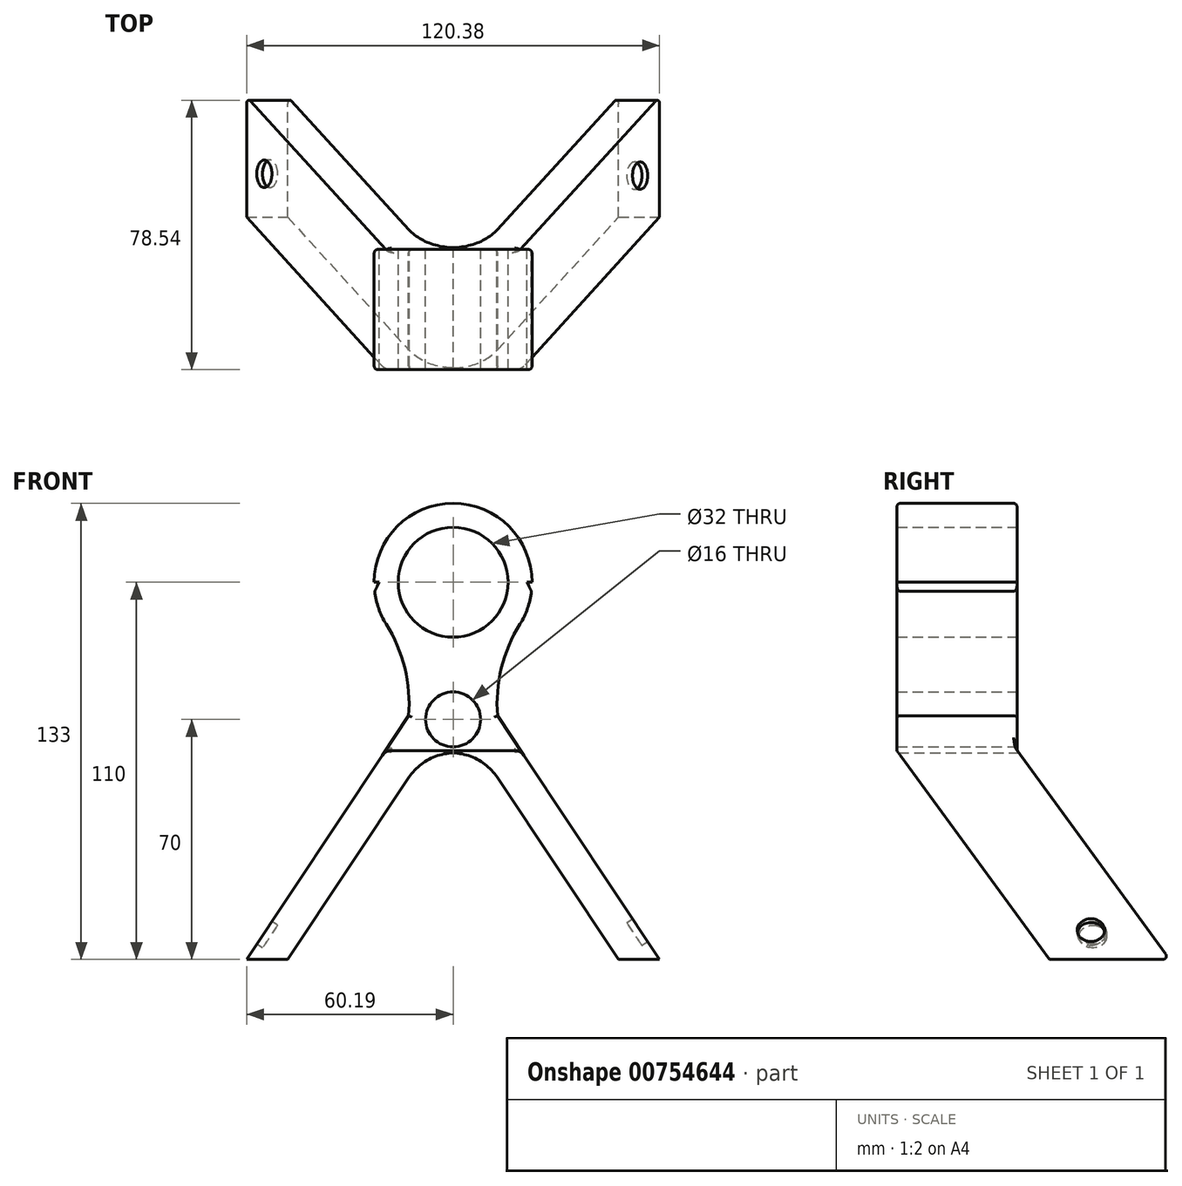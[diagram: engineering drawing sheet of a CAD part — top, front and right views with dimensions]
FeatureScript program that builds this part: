
annotation { "Feature Type Name" : "Feature", "Feature Type Description" : "" }
export const myFeature = defineFeature(function(context is Context, id is Id, definition is map)
    precondition{}
    {
        {
            var Q0;
            Q0=qCreatedBy(makeId("Front.planeOp"),FACE);
            var sketch = newSketch(context, id + "F0", { "sketchPlane" : qUnion([Q0])});
            skCircle(sketch, "E0", {"center": v(0, 0) * mm, "radius": 16 * mm});
            skArc(sketch, "E1", {"start": v(19.5, -12.19) * mm, "mid": v(0, 23) * mm, "end": v(-19.5, -12.19) * mm});
            skCircle(sketch, "E2", {"center": v(0, -40) * mm, "radius": 8 * mm});
            skArc(sketch, "E3", {"start": v(-12.96, -38.97) * mm, "mid": v(-14.08, -25.05) * mm, "end": v(-19.5, -12.19) * mm});
            skLineSegment(sketch, "E4", {"start": v(0, 30.6) * mm, "end": v(0, -110) * mm, "construction": true});
            skArc(sketch, "E5.MirrorCS", {"start": v(12.96, -38.97) * mm, "mid": v(14.08, -25.05) * mm, "end": v(19.5, -12.19) * mm});
            skLineSegment(sketch, "E6", {"start": v(-12.96, -38.97) * mm, "end": v(-60.19, -110) * mm});
            skLineSegment(sketch, "E7", {"start": v(-60.19, -110) * mm, "end": v(-48.18, -110) * mm});
            skLineSegment(sketch, "E8", {"start": v(-48.18, -110) * mm, "end": v(-12.87, -56.9) * mm});
            skArc(sketch, "E9", {"start": v(0, -49.76) * mm, "mid": v(-7.3, -51.76) * mm, "end": v(-12.87, -56.9) * mm});
            skArc(sketch, "E10.MirrorCS", {"start": v(0, -49.76) * mm, "mid": v(7.3, -51.76) * mm, "end": v(12.87, -56.9) * mm});
            skLineSegment(sketch, "E11.MirrorCS", {"start": v(48.18, -110) * mm, "end": v(12.87, -56.9) * mm});
            skLineSegment(sketch, "E12.MirrorCS", {"start": v(60.19, -110) * mm, "end": v(48.18, -110) * mm});
            skLineSegment(sketch, "E13.MirrorCS", {"start": v(12.96, -38.97) * mm, "end": v(60.19, -110) * mm});
            skPoint(sketch, "E14.orphan", {"position": v(-8.3, -50.01) * mm});
            skPoint(sketch, "E15.orphan", {"position": v(8.3, -50.01) * mm});
            skLineSegment(sketch, "E16.trimOffspring", {"start": v(0, -49.76) * mm, "end": v(0, -49.76) * mm});
            skPoint(sketch, "E17", {"position": v(0, -110) * mm});
            skSolve(sketch);
        }
        {
            var Q0;
            Q0=makeQuery(id+"F0.imprint","IMPRINT",FACE,{"disambiguationData":[TD([[makeQuery(id+"F0.imprint","IMPRINT",EDGE,{"derivedFrom":sQuery(id+"F0.wireOp",EDGE,"E0")}),-1.0]])]});
            extrude(context, id + "F1", {"entities" : qUnion([Q0]), "depth" : 80 * mm, "offsetDistance" : 25 * mm});
        }
        {
            var Q0;
            Q0=qCreatedBy(makeId("Right.planeOp"),FACE);
            var sketch = newSketch(context, id + "F2", { "sketchPlane" : qUnion([Q0])});
            skLineSegment(sketch, "E18", {"start": v(-45, 71.26) * mm, "end": v(-45, -49) * mm});
            skLineSegment(sketch, "E19", {"start": v(-45, -49) * mm, "end": v(19.32, -137.16) * mm});
            skLineSegment(sketch, "E20", {"start": v(19.32, -137.16) * mm, "end": v(19.32, 71.26) * mm});
            skLineSegment(sketch, "E21", {"start": v(19.32, 71.26) * mm, "end": v(-45, 71.26) * mm});
            skLineSegment(sketch, "E22", {"start": v(-93.3, -49) * mm, "end": v(-80.1, -49) * mm});
            skLineSegment(sketch, "E23", {"start": v(-80.1, -49) * mm, "end": v(-13.1, -140.85) * mm});
            skLineSegment(sketch, "E24", {"start": v(-13.1, -140.85) * mm, "end": v(-93.3, -140.85) * mm});
            skLineSegment(sketch, "E25", {"start": v(-93.3, -140.85) * mm, "end": v(-93.3, -49) * mm});
            skSolve(sketch);
        }
        {
            var Q0;
            Q0 = qSketchRegion(id + "F2", true);
            extrude(context, id + "F3", {"entities" : qUnion([Q0]), "operationType" : NewBodyOperationType.REMOVE, "endBound" : BoundingType.THROUGH_ALL, "oppositeDirection" : true, "depth" : 25 * mm, "offsetDistance" : 25 * mm});
        }
        {
            var Q0;
            Q0 = qSketchRegion(id + "F2", true);
            extrude(context, id + "F4", {"entities" : qUnion([Q0]), "operationType" : NewBodyOperationType.REMOVE, "endBound" : BoundingType.THROUGH_ALL, "depth" : 25 * mm, "offsetDistance" : 25 * mm});
        }
        {
            var Q0;
            Q0=makeQuery(id+"F1.opExtrude","CAP_EDGE",EDGE,{"disambiguationData":[OSD([sQuery(id+"F0.wireOp",EDGE,"E1")])],"isStart":false});
            var Q1;
            Q1=makeQuery(id+"F1.opExtrude","CAP_EDGE",EDGE,{"disambiguationData":[OSD([sQuery(id+"F0.wireOp",EDGE,"E6")])],"isStart":false});
            var Q2;
            Q2=makeQuery(id+"F1.opExtrude","CAP_EDGE",EDGE,{"disambiguationData":[OSD([sQuery(id+"F0.wireOp",EDGE,"E13.MirrorCS")])],"isStart":false});
            var Q3;
            Q3=makeQuery(id+"F4.boolean.opBoolean","INTERSECT",EDGE,{"derivedFrom":[makeQuery(id+"F1.opExtrude","SWEPT_FACE",FACE,{"disambiguationData":[OSD([sQuery(id+"F0.wireOp",EDGE,"E1")])]}),makeQuery(id+"F4.opExtrude","SWEPT_FACE",FACE,{"disambiguationData":[OSD([sQuery(id+"F2.wireOp",EDGE,"E18")])]})]});
            var Q4;
            Q4=makeQuery(id+"F4.boolean.opBoolean","INTERSECT",EDGE,{"derivedFrom":[makeQuery(id+"F1.opExtrude","SWEPT_FACE",FACE,{"disambiguationData":[OSD([sQuery(id+"F0.wireOp",EDGE,"E13.MirrorCS")])]}),makeQuery(id+"F4.opExtrude","SWEPT_FACE",FACE,{"disambiguationData":[OSD([sQuery(id+"F2.wireOp",EDGE,"E18")])]})]});
            var Q5;
            Q5=makeQuery(id+"F3.boolean.opBoolean","INTERSECT",EDGE,{"derivedFrom":[makeQuery(id+"F1.opExtrude","SWEPT_FACE",FACE,{"disambiguationData":[OSD([sQuery(id+"F0.wireOp",EDGE,"E7")])]}),makeQuery(id+"F3.opExtrude","SWEPT_FACE",FACE,{"disambiguationData":[OSD([sQuery(id+"F2.wireOp",EDGE,"E19")])]})]});
            var Q6;
            Q6=makeQuery(id+"F4.boolean.opBoolean","INTERSECT",EDGE,{"derivedFrom":[makeQuery(id+"F1.opExtrude","SWEPT_FACE",FACE,{"disambiguationData":[OSD([sQuery(id+"F0.wireOp",EDGE,"E12.MirrorCS")])]}),makeQuery(id+"F4.opExtrude","SWEPT_FACE",FACE,{"disambiguationData":[OSD([sQuery(id+"F2.wireOp",EDGE,"E19")])]})]});
            var Q7;
            Q7=makeQuery(id+"F3.boolean.opBoolean","INTERSECT",EDGE,{"derivedFrom":[makeQuery(id+"F1.opExtrude","SWEPT_FACE",FACE,{"disambiguationData":[OSD([sQuery(id+"F0.wireOp",EDGE,"E6")])]}),makeQuery(id+"F3.opExtrude","SWEPT_FACE",FACE,{"disambiguationData":[OSD([sQuery(id+"F2.wireOp",EDGE,"E18")])]})]});
            fillet(context, id + "F5", {"entities" : qUnion([Q0, Q1, Q2, Q3, Q4, Q5, Q6, Q7]), "radius" : 1 * mm, "tangentPropagation" : true, "allowEdgeOverflow" : false});
        }
        {
            var Q0;
            {var subQ0=sQuery(id+"F2.wireOp",EDGE,"E19");var subQ1=sQuery(id+"F2.wireOp",EDGE,"E18");Q0=makeQuery(id+"F4.boolean.opBoolean","MERGE",EDGE,{"derivedFrom":[makeQuery(id+"F3.boolean.opBoolean","COPY",EDGE,{"derivedFrom":makeQuery(id+"F3.opExtrude","SWEPT_EDGE",EDGE,{"disambiguationData":[OSD([subQ1,subQ0])]})}),makeQuery(id+"F4.opExtrude","SWEPT_EDGE",EDGE,{"disambiguationData":[OSD([subQ1,subQ0])]})]});}
            fillet(context, id + "F6", {"entities" : qUnion([Q0]), "radius" : 2 * mm, "tangentPropagation" : true, "allowEdgeOverflow" : false});
        }
        {
            var Q0;
            Q0=qCreatedBy(makeId("Front.planeOp"),FACE);
            var sketch = newSketch(context, id + "F7", { "sketchPlane" : qUnion([Q0])});
            skCircle(sketch, "E26", {"center": v(0, 0) * mm, "radius": 16 * mm, "construction": true});
            skArc(sketch, "E27", {"start": v(19.5, -12.19) * mm, "mid": v(0, 23) * mm, "end": v(-19.5, -12.19) * mm, "construction": true});
            skCircle(sketch, "E28", {"center": v(0, -40) * mm, "radius": 8 * mm, "construction": true});
            skArc(sketch, "E29", {"start": v(-12.96, -38.97) * mm, "mid": v(-14.08, -25.05) * mm, "end": v(-19.5, -12.19) * mm, "construction": true});
            skLineSegment(sketch, "E30", {"start": v(0, 77.13) * mm, "end": v(0, -110) * mm, "construction": true});
            skArc(sketch, "E31.MirrorCS", {"start": v(12.96, -38.97) * mm, "mid": v(14.08, -25.05) * mm, "end": v(19.5, -12.19) * mm, "construction": true});
            skLineSegment(sketch, "E32", {"start": v(-12.96, -38.97) * mm, "end": v(-60.19, -110) * mm, "construction": true});
            skLineSegment(sketch, "E33", {"start": v(-60.19, -110) * mm, "end": v(-48.18, -110) * mm, "construction": true});
            skLineSegment(sketch, "E34", {"start": v(-48.18, -110) * mm, "end": v(-12.87, -56.9) * mm, "construction": true});
            skArc(sketch, "E35", {"start": v(0, -49.76) * mm, "mid": v(-7.3, -51.76) * mm, "end": v(-12.87, -56.9) * mm, "construction": true});
            skArc(sketch, "E36.MirrorCS", {"start": v(0, -49.76) * mm, "mid": v(7.3, -51.76) * mm, "end": v(12.87, -56.9) * mm, "construction": true});
            skLineSegment(sketch, "E37.MirrorCS", {"start": v(48.18, -110) * mm, "end": v(12.87, -56.9) * mm, "construction": true});
            skLineSegment(sketch, "E38.MirrorCS", {"start": v(60.19, -110) * mm, "end": v(48.18, -110) * mm, "construction": true});
            skLineSegment(sketch, "E39.MirrorCS", {"start": v(12.96, -38.97) * mm, "end": v(60.19, -110) * mm, "construction": true});
            skPoint(sketch, "E40.orphan", {"position": v(-8.3, -50.01) * mm});
            skPoint(sketch, "E41.orphan", {"position": v(8.3, -50.01) * mm});
            skLineSegment(sketch, "E42.trimOffspring", {"start": v(0, -49.76) * mm, "end": v(0, -49.76) * mm});
            skPoint(sketch, "E43", {"position": v(0, -110) * mm});
            skLineSegment(sketch, "E44", {"start": v(-25.8, 0) * mm, "end": v(-21.56, 0) * mm});
            skLineSegment(sketch, "E45", {"start": v(-21.56, 0) * mm, "end": v(-25.13, -7.48) * mm});
            skLineSegment(sketch, "E46", {"start": v(-25.13, -7.48) * mm, "end": v(-25.8, 0) * mm});
            skLineSegment(sketch, "E47.MirrorCS", {"start": v(25.8, 0) * mm, "end": v(21.56, 0) * mm});
            skLineSegment(sketch, "E48.MirrorCS", {"start": v(21.56, 0) * mm, "end": v(25.13, -7.48) * mm});
            skLineSegment(sketch, "E49.MirrorCS", {"start": v(25.13, -7.48) * mm, "end": v(25.8, 0) * mm});
            skSolve(sketch);
        }
        {
            var Q0;
            Q0 = qSketchRegion(id + "F7", true);
            extrude(context, id + "F8", {"entities" : qUnion([Q0]), "operationType" : NewBodyOperationType.REMOVE, "endBound" : BoundingType.THROUGH_ALL, "depth" : 25 * mm, "offsetDistance" : 25 * mm});
        }
        {
            var Q0;
            Q0=makeQuery(id+"F1.opExtrude","SWEPT_FACE",FACE,{"disambiguationData":[OSD([sQuery(id+"F0.wireOp",EDGE,"E6")])]});
            var sketch = newSketch(context, id + "F9", { "sketchPlane" : qUnion([Q0])});
            skCircle(sketch, "E50", {"center": v(22.92, -115.58) * mm, "radius": 4 * mm});
            skSolve(sketch);
        }
        {
            var Q0;
            Q0 = qSketchRegion(id + "F9", true);
            extrude(context, id + "F10", {"entities" : qUnion([Q0]), "operationType" : NewBodyOperationType.REMOVE, "oppositeDirection" : true, "depth" : 2 * mm, "offsetDistance" : 25 * mm});
        }
        {
            var Q0;
            Q0=makeQuery(id+"F1.opExtrude","SWEPT_FACE",FACE,{"disambiguationData":[OSD([sQuery(id+"F0.wireOp",EDGE,"E13.MirrorCS")])]});
            var sketch = newSketch(context, id + "F11", { "sketchPlane" : qUnion([Q0])});
            skCircle(sketch, "E51", {"center": v(-23.44, -114.66) * mm, "radius": 4 * mm});
            skSolve(sketch);
        }
        {
            var Q0;
            Q0 = qSketchRegion(id + "F11", true);
            extrude(context, id + "F12", {"entities" : qUnion([Q0]), "operationType" : NewBodyOperationType.REMOVE, "oppositeDirection" : true, "depth" : 2 * mm, "offsetDistance" : 25 * mm});
        }
    });
